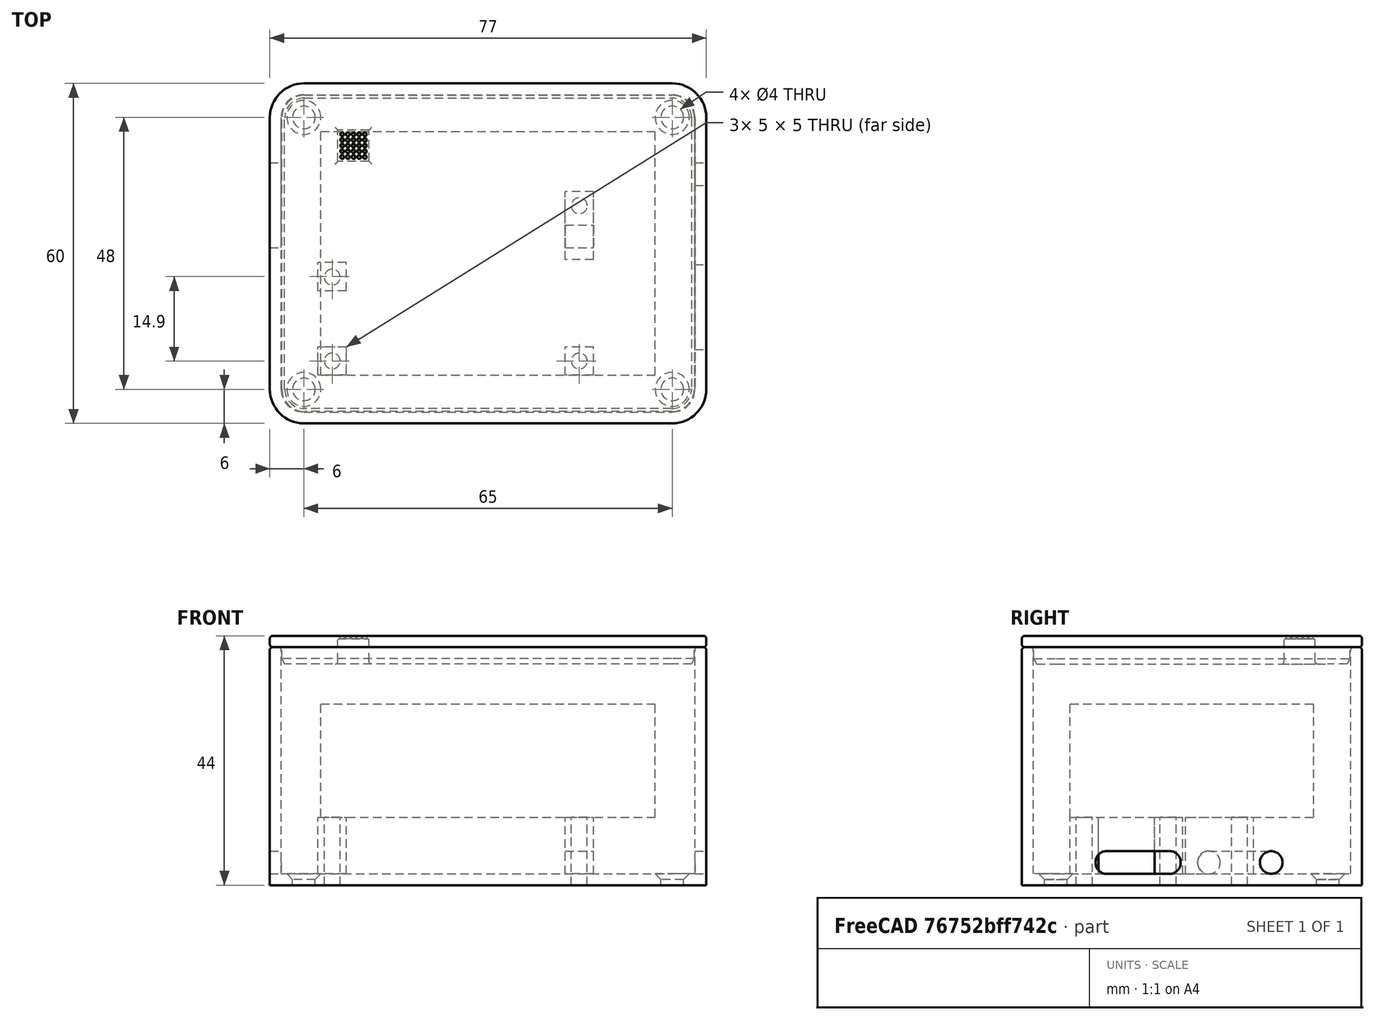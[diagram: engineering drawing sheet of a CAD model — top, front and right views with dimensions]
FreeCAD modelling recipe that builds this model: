
FCSTD DOCUMENT  (FreeCAD 0.18R4 (GitTag))
Label: DriverCase
License: All rights reserved
LicenseURL: http://en.wikipedia.org/wiki/All_rights_reserved
objects: Part::Cone×25, Part::Box×12, Part::Cylinder×10, Part::Fillet×9, Part::MultiFuse×9, Part::Cut×4, Part::Chamfer×2
note: 71 computed .brp shape members not serialized (recipe doc carries the construction recipe); baked Part::Feature solids carry a one-line shape summary decoded from their .brp

FEATURE [Part::Box] Box  label="Innenraum"
  AttacherType = Attacher::AttachEngine3D
  Height = 40
  Length = 73
  Placement = pos=(-37,-28,2) rot=(0,0,1;0rad)
  Width = 56
FEATURE [Part::Box] Box001  label="Umrandung"
  AttacherType = Attacher::AttachEngine3D
  Height = 42
  Length = 77
  Placement = pos=(-39,-30,0) rot=(0,0,1;0rad)
  Width = 60
FEATURE [Part::Box] Box002  label="MotorShild"
  AttacherType = Attacher::AttachEngine3D
  Height = 20
  Length = 59
  Placement = pos=(-30,-21.5,12) rot=(0,0,1;0rad)
  Width = 43
FEATURE [Part::Cylinder] Cylinder004  label="Zylinder"
  Angle = 360
  AttacherType = Attacher::AttachEngine3D
  Height = 40
  Placement = pos=(32,24,0) rot=(0,0,1;0rad)
  Radius = 2
FEATURE [Part::Cylinder] Cylinder005  label="Zylinder001"
  Angle = 360
  AttacherType = Attacher::AttachEngine3D
  Height = 40
  Placement = pos=(32,-24,0) rot=(0,0,1;0rad)
  Radius = 2
FEATURE [Part::Cylinder] Cylinder006  label="Zylinder002"
  Angle = 360
  AttacherType = Attacher::AttachEngine3D
  Height = 40
  Placement = pos=(-33,24,0) rot=(0,0,1;0rad)
  Radius = 2
FEATURE [Part::Cylinder] Cylinder007  label="Zylinder003"
  Angle = 360
  AttacherType = Attacher::AttachEngine3D
  Height = 40
  Placement = pos=(-33,-24,0) rot=(0,0,1;0rad)
  Radius = 2
FEATURE [Part::Fillet] Fillet  label="InnenraumRund"
  Base = -> Box
  Edges = 4 edges r=4: [Edge1,Edge3,Edge5,Edge7]
FEATURE [Part::Fillet] Fillet001  label="UmrandungRund"
  Base = -> Box001
  Edges = 4 edges r=6: [Edge1,Edge3,Edge5,Edge7]
FEATURE [Part::Cut] Cut
  Base = -> Fillet001
  Tool = -> Fillet
FEATURE [Part::Box] Box003  label="Würfel"
  AttacherType = Attacher::AttachEngine3D
  Height = 4
  Length = 2
  Placement = pos=(36,-17,2) rot=(0,0,1;0rad)
  Width = 15
FEATURE [Part::Cylinder] Cylinder  label="Zylinder004"
  Angle = 360
  AttacherType = Attacher::AttachEngine3D
  Height = 10
  Placement = pos=(32,14,4) rot=(0,1,0;1.5708rad)
  Radius = 2
FEATURE [Part::Box] Box004  label="Würfel001"
  AttacherType = Attacher::AttachEngine3D
  Height = 4
  Length = 2
  Placement = pos=(-39,1,2) rot=(0,0,1;0rad)
  Width = 15
FEATURE [Part::Fillet] Fillet002
  Base = -> Box004
  Edges = 4 edges r=1.9: [Edge9,Edge10,Edge11,Edge12]
FEATURE [Part::Fillet] Fillet003
  Base = -> Box003
  Edges = 4 edges r=1.9: [Edge9,Edge10,Edge11,Edge12]
FEATURE [Part::Box] Box005  label="HalterBodyLU"
  AttacherType = Attacher::AttachEngine3D
  Height = 12
  Length = 5
  Placement = pos=(-30.5,-21.5,0) rot=(0,0,1;0rad)
  Width = 5
FEATURE [Part::Box] Box006  label="HalterBodyRU"
  AttacherType = Attacher::AttachEngine3D
  Height = 12
  Length = 5
  Placement = pos=(13.1,-21.5,0) rot=(0,0,1;0rad)
  Width = 5
FEATURE [Part::Box] Box007  label="HalterBodyRO"
  AttacherType = Attacher::AttachEngine3D
  Height = 12
  Length = 5
  Placement = pos=(13.1,-1.1,0) rot=(0,0,1;0rad)
  Width = 12
FEATURE [Part::Box] Box008  label="HalterBodyLO"
  AttacherType = Attacher::AttachEngine3D
  Height = 12
  Length = 5
  Placement = pos=(-30.5,-6.6,0) rot=(0,0,1;0rad)
  Width = 5
FEATURE [Part::Cylinder] Cylinder008  label="HalterLochLU"
  Angle = 360
  AttacherType = Attacher::AttachEngine3D
  Height = 14
  Placement = pos=(-28,-19,0) rot=(0,0,1;0rad)
  Radius = 1.4
FEATURE [Part::Cylinder] Cylinder009  label="HalterLochRU"
  Angle = 360
  AttacherType = Attacher::AttachEngine3D
  Height = 14
  Placement = pos=(15.6,-19,0) rot=(0,0,1;0rad)
  Radius = 1.4
FEATURE [Part::Cylinder] Cylinder010  label="HalterLochRO"
  Angle = 360
  AttacherType = Attacher::AttachEngine3D
  Height = 14
  Placement = pos=(15.6,8.4,0) rot=(0,0,1;0rad)
  Radius = 1.4
FEATURE [Part::Cylinder] Cylinder011  label="HalterLochLO"
  Angle = 360
  AttacherType = Attacher::AttachEngine3D
  Height = 14
  Placement = pos=(-28,-4.2,0) rot=(0,0,1;0rad)
  Radius = 1.4
FEATURE [Part::Cylinder] Cylinder012  label="Zylinder005"
  Angle = 360
  AttacherType = Attacher::AttachEngine3D
  Height = 10
  Placement = pos=(11,3,4) rot=(0,1,0;1.5708rad)
  Radius = 2
FEATURE [Part::Cut] Cut001
  Base = -> Box007
  Tool = -> Cylinder012
FEATURE [Part::MultiFuse] Fusion001
  Shapes = -> [Cut,Box005,Box006,Box008,Cut001]
FEATURE [Part::MultiFuse] Fusion
  Shapes = -> [Cylinder008,Cylinder011,Cylinder010,Cylinder009,Cylinder004,Cylinder005,Cylinder006,Cylinder007,Cylinder,Fillet002,Fillet003]
FEATURE [Part::Cut] Cut002
  Base = -> Fusion001
  Tool = -> Fusion
FEATURE [Part::Chamfer] Chamfer
  Base = -> Cut002
  Edges = 4 edges r=1: [Edge65,Edge70,Edge72,Edge74]
FEATURE [Part::Fillet] Fillet004  label="Unterbau"
  Base = -> Chamfer
  Edges = 16 edges r=0.5: [Edge68,Edge80,Edge82,Edge84,Edge86,Edge88,Edge90,Edge91,Edge111,Edge122,Edge126,Edge128,Edge130,Edge131,Edge142,Edge145]
FEATURE [Part::Box] Box009  label="Innenraum001"
  AttacherType = Attacher::AttachEngine3D
  Height = 3
  Length = 72.8
  Placement = pos=(-36.9,-27.9,39) rot=(0,0,1;0rad)
  Width = 55.8
FEATURE [Part::Box] Box010  label="Umrandung001"
  AttacherType = Attacher::AttachEngine3D
  Height = 2
  Length = 77
  Placement = pos=(-39,-30,42) rot=(0,0,1;0rad)
  Width = 60
FEATURE [Part::Fillet] Fillet005  label="InnenraumRund001"
  Base = -> Box009
  Edges = 4 edges r=4: [Edge1,Edge3,Edge5,Edge7]
FEATURE [Part::Fillet] Fillet006  label="UmrandungRund001"
  Base = -> Box010
  Edges = 4 edges r=6: [Edge1,Edge3,Edge5,Edge7]
FEATURE [Part::Chamfer] Chamfer001
  Base = -> Fillet005
  Edges = 8 edges: [Edge4 r1=1 r2=0.5,Edge12 r1=1 r2=0.5,Edge14 r1=1 r2=0.5,Edge16 r1=1 r2=0.5,Edge17 r1=1 r2=0.5,Edge18 r1=1 r2=0.5,Edge19 r1=1 r2=0.5,Edge20 r1=1 r2=0.5]
FEATURE [Part::Fillet] Fillet007
  Base = -> Fillet006
  Edges = 16 edges r=0.5: [Edge1,Edge4,Edge5,Edge6,Edge7,Edge8,Edge9,Edge10,Edge11,Edge12,Edge14,Edge16,Edge17,Edge18,Edge19,Edge20]
FEATURE [Part::Box] Box011  label="Würfel002"
  AttacherType = Attacher::AttachEngine3D
  Height = 10
  Length = 5.5
  Placement = pos=(-27,16.25,33.5) rot=(0,0,1;0rad)
  Width = 5.5
FEATURE [Part::MultiFuse] Fusion002  label="DeckelRund"
  Shapes = -> [Chamfer001,Fillet007]
FEATURE [Part::Cone] Cone  label="Kegel"
  Angle = 360
  AttacherType = Attacher::AttachEngine3D
  Height = 1
  Placement = pos=(-24.25,19,44) rot=(1,0,0;3.14159rad)
  Radius1 = 0.3
  Radius2 = 0.6
FEATURE [Part::Cone] Cone001  label="Kegel001"
  Angle = 360
  AttacherType = Attacher::AttachEngine3D
  Height = 1
  Placement = pos=(-25.25,19,44) rot=(1,0,0;3.14159rad)
  Radius1 = 0.3
  Radius2 = 0.6
FEATURE [Part::Cone] Cone002  label="Kegel002"
  Angle = 360
  AttacherType = Attacher::AttachEngine3D
  Height = 1
  Placement = pos=(-26.25,19,44) rot=(1,0,0;3.14159rad)
  Radius1 = 0.3
  Radius2 = 0.6
FEATURE [Part::Cone] Cone003  label="Kegel003"
  Angle = 360
  AttacherType = Attacher::AttachEngine3D
  Height = 1
  Placement = pos=(-23.25,19,44) rot=(1,0,0;3.14159rad)
  Radius1 = 0.3
  Radius2 = 0.6
FEATURE [Part::Cone] Cone004  label="Kegel004"
  Angle = 360
  AttacherType = Attacher::AttachEngine3D
  Height = 1
  Placement = pos=(-22.25,19,44) rot=(1,0,0;3.14159rad)
  Radius1 = 0.3
  Radius2 = 0.6
FEATURE [Part::MultiFuse] Fusion003
  Shapes = -> [Cone,Cone001,Cone003,Cone004,Cone002]
FEATURE [Part::Cone] Cone005  label="Kegel005"
  Angle = 360
  AttacherType = Attacher::AttachEngine3D
  Height = 1
  Placement = pos=(-25.25,19,44) rot=(1,0,0;3.14159rad)
  Radius1 = 0.3
  Radius2 = 0.6
FEATURE [Part::Cone] Cone006  label="Kegel006"
  Angle = 360
  AttacherType = Attacher::AttachEngine3D
  Height = 1
  Placement = pos=(-24.25,19,44) rot=(1,0,0;3.14159rad)
  Radius1 = 0.3
  Radius2 = 0.6
FEATURE [Part::Cone] Cone007  label="Kegel007"
  Angle = 360
  AttacherType = Attacher::AttachEngine3D
  Height = 1
  Placement = pos=(-23.25,19,44) rot=(1,0,0;3.14159rad)
  Radius1 = 0.3
  Radius2 = 0.6
FEATURE [Part::Cone] Cone008  label="Kegel008"
  Angle = 360
  AttacherType = Attacher::AttachEngine3D
  Height = 1
  Placement = pos=(-22.25,19,44) rot=(1,0,0;3.14159rad)
  Radius1 = 0.3
  Radius2 = 0.6
FEATURE [Part::Cone] Cone009  label="Kegel009"
  Angle = 360
  AttacherType = Attacher::AttachEngine3D
  Height = 1
  Placement = pos=(-26.25,19,44) rot=(1,0,0;3.14159rad)
  Radius1 = 0.3
  Radius2 = 0.6
FEATURE [Part::MultiFuse] Fusion004
  Placement = pos=(0,1,0) rot=(0,0,1;0rad)
  Shapes = -> [Cone006,Cone005,Cone007,Cone008,Cone009]
FEATURE [Part::Cone] Cone010  label="Kegel010"
  Angle = 360
  AttacherType = Attacher::AttachEngine3D
  Height = 1
  Placement = pos=(-25.25,19,44) rot=(1,0,0;3.14159rad)
  Radius1 = 0.3
  Radius2 = 0.6
FEATURE [Part::Cone] Cone011  label="Kegel011"
  Angle = 360
  AttacherType = Attacher::AttachEngine3D
  Height = 1
  Placement = pos=(-24.25,19,44) rot=(1,0,0;3.14159rad)
  Radius1 = 0.3
  Radius2 = 0.6
FEATURE [Part::Cone] Cone012  label="Kegel012"
  Angle = 360
  AttacherType = Attacher::AttachEngine3D
  Height = 1
  Placement = pos=(-23.25,19,44) rot=(1,0,0;3.14159rad)
  Radius1 = 0.3
  Radius2 = 0.6
FEATURE [Part::Cone] Cone013  label="Kegel013"
  Angle = 360
  AttacherType = Attacher::AttachEngine3D
  Height = 1
  Placement = pos=(-22.25,19,44) rot=(1,0,0;3.14159rad)
  Radius1 = 0.3
  Radius2 = 0.6
FEATURE [Part::Cone] Cone014  label="Kegel014"
  Angle = 360
  AttacherType = Attacher::AttachEngine3D
  Height = 1
  Placement = pos=(-26.25,19,44) rot=(1,0,0;3.14159rad)
  Radius1 = 0.3
  Radius2 = 0.6
FEATURE [Part::MultiFuse] Fusion005
  Placement = pos=(0,2,0) rot=(0,0,1;0rad)
  Shapes = -> [Cone011,Cone010,Cone012,Cone013,Cone014]
FEATURE [Part::Cone] Cone015  label="Kegel015"
  Angle = 360
  AttacherType = Attacher::AttachEngine3D
  Height = 1
  Placement = pos=(-25.25,19,44) rot=(1,0,0;3.14159rad)
  Radius1 = 0.3
  Radius2 = 0.6
FEATURE [Part::Cone] Cone016  label="Kegel016"
  Angle = 360
  AttacherType = Attacher::AttachEngine3D
  Height = 1
  Placement = pos=(-24.25,19,44) rot=(1,0,0;3.14159rad)
  Radius1 = 0.3
  Radius2 = 0.6
FEATURE [Part::Cone] Cone017  label="Kegel017"
  Angle = 360
  AttacherType = Attacher::AttachEngine3D
  Height = 1
  Placement = pos=(-23.25,19,44) rot=(1,0,0;3.14159rad)
  Radius1 = 0.3
  Radius2 = 0.6
FEATURE [Part::Cone] Cone018  label="Kegel018"
  Angle = 360
  AttacherType = Attacher::AttachEngine3D
  Height = 1
  Placement = pos=(-22.25,19,44) rot=(1,0,0;3.14159rad)
  Radius1 = 0.3
  Radius2 = 0.6
FEATURE [Part::Cone] Cone019  label="Kegel019"
  Angle = 360
  AttacherType = Attacher::AttachEngine3D
  Height = 1
  Placement = pos=(-26.25,19,44) rot=(1,0,0;3.14159rad)
  Radius1 = 0.3
  Radius2 = 0.6
FEATURE [Part::MultiFuse] Fusion006
  Placement = pos=(0,-1,0) rot=(0,0,1;0rad)
  Shapes = -> [Cone016,Cone015,Cone017,Cone018,Cone019]
FEATURE [Part::Cone] Cone020  label="Kegel020"
  Angle = 360
  AttacherType = Attacher::AttachEngine3D
  Height = 1
  Placement = pos=(-25.25,19,44) rot=(1,0,0;3.14159rad)
  Radius1 = 0.3
  Radius2 = 0.6
FEATURE [Part::Cone] Cone021  label="Kegel021"
  Angle = 360
  AttacherType = Attacher::AttachEngine3D
  Height = 1
  Placement = pos=(-24.25,19,44) rot=(1,0,0;3.14159rad)
  Radius1 = 0.3
  Radius2 = 0.6
FEATURE [Part::Cone] Cone022  label="Kegel022"
  Angle = 360
  AttacherType = Attacher::AttachEngine3D
  Height = 1
  Placement = pos=(-23.25,19,44) rot=(1,0,0;3.14159rad)
  Radius1 = 0.3
  Radius2 = 0.6
FEATURE [Part::Cone] Cone023  label="Kegel023"
  Angle = 360
  AttacherType = Attacher::AttachEngine3D
  Height = 1
  Placement = pos=(-22.25,19,44) rot=(1,0,0;3.14159rad)
  Radius1 = 0.3
  Radius2 = 0.6
FEATURE [Part::Cone] Cone024  label="Kegel024"
  Angle = 360
  AttacherType = Attacher::AttachEngine3D
  Height = 1
  Placement = pos=(-26.25,19,44) rot=(1,0,0;3.14159rad)
  Radius1 = 0.3
  Radius2 = 0.6
FEATURE [Part::MultiFuse] Fusion007
  Placement = pos=(0,-2,0) rot=(0,0,1;0rad)
  Shapes = -> [Cone021,Cone020,Cone022,Cone023,Cone024]
FEATURE [Part::MultiFuse] Fusion008  label="WS2812"
  Shapes = -> [Fusion003,Fusion004,Fusion007,Fusion005,Fusion006,Box011]
FEATURE [Part::Cut] Cut003
  Base = -> Fusion002
  Tool = -> Fusion008
FEATURE [Part::Fillet] Fillet008  label="Deckel"
  Base = -> Cut003
  Edges = 4 edges r=0.5: [Edge176,Edge177,Edge178,Edge179]
